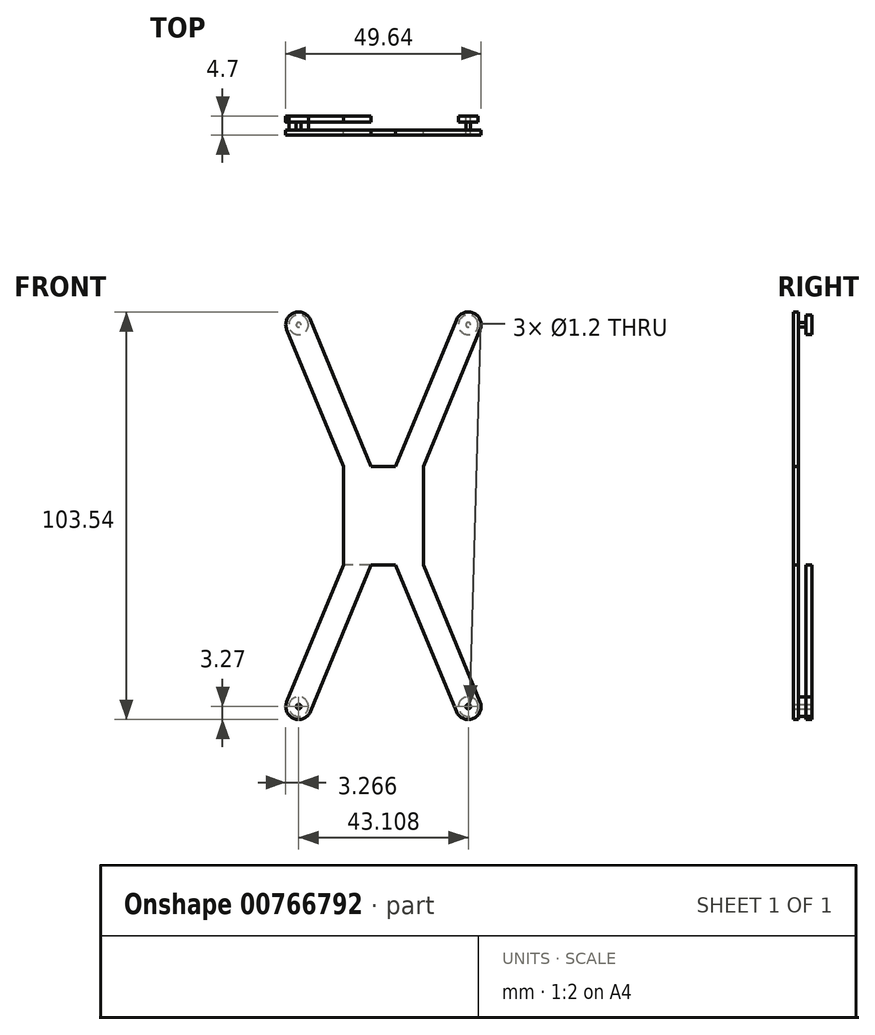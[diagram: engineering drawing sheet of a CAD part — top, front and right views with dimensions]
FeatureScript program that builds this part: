
annotation { "Feature Type Name" : "Feature", "Feature Type Description" : "" }
export const myFeature = defineFeature(function(context is Context, id is Id, definition is map)
    precondition{}
    {
        {
            var Q0;
            Q0=qCreatedBy(makeId("Front.planeOp"),FACE);
            var sketch = newSketch(context, id + "F0", { "sketchPlane" : qUnion([Q0])});
            skLineSegment(sketch, "E0", {"start": v(-5, 0) * mm, "end": v(-24.57, 47.25) * mm});
            skLineSegment(sketch, "E1", {"start": v(-24.57, 47.25) * mm, "end": v(-18.54, 49.75) * mm});
            skLineSegment(sketch, "E2", {"start": v(-18.54, 49.75) * mm, "end": v(0, 5) * mm});
            skLineSegment(sketch, "E3", {"start": v(0, 5) * mm, "end": v(18.54, 49.75) * mm});
            skLineSegment(sketch, "E4", {"start": v(18.54, 49.75) * mm, "end": v(24.57, 47.25) * mm});
            skLineSegment(sketch, "E5", {"start": v(24.57, 47.25) * mm, "end": v(5, 0) * mm});
            skLineSegment(sketch, "E6", {"start": v(5, 0) * mm, "end": v(24.57, -47.25) * mm});
            skLineSegment(sketch, "E7", {"start": v(24.57, -47.25) * mm, "end": v(18.54, -49.75) * mm});
            skLineSegment(sketch, "E8", {"start": v(18.54, -49.75) * mm, "end": v(0, -5) * mm});
            skLineSegment(sketch, "E9", {"start": v(0, -5) * mm, "end": v(-18.54, -49.75) * mm});
            skLineSegment(sketch, "E10", {"start": v(-18.54, -49.75) * mm, "end": v(-24.57, -47.25) * mm});
            skLineSegment(sketch, "E11", {"start": v(-24.57, -47.25) * mm, "end": v(-5, 0) * mm});
            skArc(sketch, "E12", {"start": v(-24.57, -47.25) * mm, "mid": v(-22.8, -51.52) * mm, "end": v(-18.54, -49.75) * mm});
            skArc(sketch, "E13", {"start": v(18.54, -49.75) * mm, "mid": v(22.8, -51.52) * mm, "end": v(24.57, -47.25) * mm});
            skArc(sketch, "E14", {"start": v(24.57, 47.25) * mm, "mid": v(22.8, 51.52) * mm, "end": v(18.54, 49.75) * mm});
            skArc(sketch, "E15", {"start": v(-18.54, 49.75) * mm, "mid": v(-22.8, 51.52) * mm, "end": v(-24.57, 47.25) * mm});
            skCircle(sketch, "E16", {"center": v(-21.55, 48.5) * mm, "radius": 0.6 * mm});
            skCircle(sketch, "E17", {"center": v(21.55, 48.5) * mm, "radius": 0.6 * mm});
            skCircle(sketch, "E18", {"center": v(-21.55, -48.5) * mm, "radius": 0.6 * mm});
            skCircle(sketch, "E19", {"center": v(21.55, -48.5) * mm, "radius": 0.6 * mm});
            skCircle(sketch, "E20", {"center": v(-21.55, -48.5) * mm, "radius": 2.5 * mm});
            skCircle(sketch, "E21", {"center": v(21.55, -48.5) * mm, "radius": 2.5 * mm});
            skCircle(sketch, "E22", {"center": v(-21.55, 48.5) * mm, "radius": 2.5 * mm});
            skCircle(sketch, "E23", {"center": v(21.55, 48.5) * mm, "radius": 2.5 * mm});
            skLineSegment(sketch, "E24.bottom", {"start": v(10.18, 12.5) * mm, "end": v(-10.18, 12.5) * mm});
            skLineSegment(sketch, "E24.top", {"start": v(10.18, -12.5) * mm, "end": v(-10.18, -12.5) * mm});
            skLineSegment(sketch, "E24.left", {"start": v(10.18, 12.5) * mm, "end": v(10.18, -12.5) * mm});
            skLineSegment(sketch, "E24.right", {"start": v(-10.18, 12.5) * mm, "end": v(-10.18, -12.5) * mm});
            skPoint(sketch, "E24.middle", {"position": v(0, 0) * mm});
            skSolve(sketch);
        }
        {
            var Q0;
            {var subQ0=sQuery(id+"F0.wireOp",EDGE,"E22");var subQ1=sQuery(id+"F0.wireOp",EDGE,"E1");var subQ2=makeQuery(id+"F0.imprint","INTERSECT",VERTEX,{"disambiguationData":[OD(0.0)],"derivedFrom":[subQ1,subQ0]});Q0=makeQuery(id+"F0.imprint","IMPRINT",FACE,{"disambiguationData":[TD([[makeQuery(id+"F0.imprint","IMPRINT",EDGE,{"disambiguationData":[TD([[subQ2,-1.0]])],"derivedFrom":subQ1}),1.0]])]});}
            var Q1;
            {var subQ0=sQuery(id+"F0.wireOp",EDGE,"E22");var subQ1=sQuery(id+"F0.wireOp",EDGE,"E1");var subQ2=makeQuery(id+"F0.imprint","INTERSECT",VERTEX,{"disambiguationData":[OD(0.0)],"derivedFrom":[subQ1,subQ0]});Q1=makeQuery(id+"F0.imprint","IMPRINT",FACE,{"disambiguationData":[TD([[makeQuery(id+"F0.imprint","IMPRINT",EDGE,{"disambiguationData":[TD([[subQ2,-1.0]])],"derivedFrom":subQ1}),-1.0]])]});}
            var Q2;
            {var subQ0=sQuery(id+"F0.wireOp",EDGE,"E16");var subQ1=sQuery(id+"F0.wireOp",EDGE,"E1");var subQ2=makeQuery(id+"F0.imprint","INTERSECT",VERTEX,{"disambiguationData":[OD(0.0)],"derivedFrom":[subQ1,subQ0]});Q2=makeQuery(id+"F0.imprint","IMPRINT",FACE,{"disambiguationData":[TD([[makeQuery(id+"F0.imprint","IMPRINT",EDGE,{"disambiguationData":[TD([[subQ2,-1.0]])],"derivedFrom":subQ1}),-1.0]])]});}
            var Q3;
            {var subQ0=sQuery(id+"F0.wireOp",EDGE,"E16");var subQ1=sQuery(id+"F0.wireOp",EDGE,"E1");var subQ2=makeQuery(id+"F0.imprint","INTERSECT",VERTEX,{"disambiguationData":[OD(0.0)],"derivedFrom":[subQ1,subQ0]});Q3=makeQuery(id+"F0.imprint","IMPRINT",FACE,{"disambiguationData":[TD([[makeQuery(id+"F0.imprint","IMPRINT",EDGE,{"disambiguationData":[TD([[subQ2,-1.0]])],"derivedFrom":subQ1}),1.0]])]});}
            var Q4;
            {var subQ0=sQuery(id+"F0.wireOp",EDGE,"E17");var subQ1=sQuery(id+"F0.wireOp",EDGE,"E4");var subQ2=makeQuery(id+"F0.imprint","INTERSECT",VERTEX,{"disambiguationData":[OD(0.0)],"derivedFrom":[subQ1,subQ0]});Q4=makeQuery(id+"F0.imprint","IMPRINT",FACE,{"disambiguationData":[TD([[makeQuery(id+"F0.imprint","IMPRINT",EDGE,{"disambiguationData":[TD([[subQ2,-1.0]])],"derivedFrom":subQ1}),1.0]])]});}
            var Q5;
            {var subQ0=sQuery(id+"F0.wireOp",EDGE,"E23");var subQ1=sQuery(id+"F0.wireOp",EDGE,"E4");var subQ2=makeQuery(id+"F0.imprint","INTERSECT",VERTEX,{"disambiguationData":[OD(0.0)],"derivedFrom":[subQ1,subQ0]});Q5=makeQuery(id+"F0.imprint","IMPRINT",FACE,{"disambiguationData":[TD([[makeQuery(id+"F0.imprint","IMPRINT",EDGE,{"disambiguationData":[TD([[subQ2,-1.0]])],"derivedFrom":subQ1}),1.0]])]});}
            var Q6;
            {var subQ0=sQuery(id+"F0.wireOp",EDGE,"E23");var subQ1=sQuery(id+"F0.wireOp",EDGE,"E4");var subQ2=makeQuery(id+"F0.imprint","INTERSECT",VERTEX,{"disambiguationData":[OD(0.0)],"derivedFrom":[subQ1,subQ0]});Q6=makeQuery(id+"F0.imprint","IMPRINT",FACE,{"disambiguationData":[TD([[makeQuery(id+"F0.imprint","IMPRINT",EDGE,{"disambiguationData":[TD([[subQ2,-1.0]])],"derivedFrom":subQ1}),-1.0]])]});}
            var Q7;
            {var subQ0=sQuery(id+"F0.wireOp",EDGE,"E17");var subQ1=sQuery(id+"F0.wireOp",EDGE,"E4");var subQ2=makeQuery(id+"F0.imprint","INTERSECT",VERTEX,{"disambiguationData":[OD(0.0)],"derivedFrom":[subQ1,subQ0]});Q7=makeQuery(id+"F0.imprint","IMPRINT",FACE,{"disambiguationData":[TD([[makeQuery(id+"F0.imprint","IMPRINT",EDGE,{"disambiguationData":[TD([[subQ2,-1.0]])],"derivedFrom":subQ1}),-1.0]])]});}
            var Q8;
            {var subQ0=sQuery(id+"F0.wireOp",EDGE,"E20");var subQ1=sQuery(id+"F0.wireOp",EDGE,"E10");var subQ2=makeQuery(id+"F0.imprint","INTERSECT",VERTEX,{"disambiguationData":[OD(0.0)],"derivedFrom":[subQ1,subQ0]});Q8=makeQuery(id+"F0.imprint","IMPRINT",FACE,{"disambiguationData":[TD([[makeQuery(id+"F0.imprint","IMPRINT",EDGE,{"disambiguationData":[TD([[subQ2,-1.0]])],"derivedFrom":subQ1}),1.0]])]});}
            var Q9;
            {var subQ0=sQuery(id+"F0.wireOp",EDGE,"E18");var subQ1=sQuery(id+"F0.wireOp",EDGE,"E10");var subQ2=makeQuery(id+"F0.imprint","INTERSECT",VERTEX,{"disambiguationData":[OD(0.0)],"derivedFrom":[subQ1,subQ0]});Q9=makeQuery(id+"F0.imprint","IMPRINT",FACE,{"disambiguationData":[TD([[makeQuery(id+"F0.imprint","IMPRINT",EDGE,{"disambiguationData":[TD([[subQ2,-1.0]])],"derivedFrom":subQ1}),1.0]])]});}
            var Q10;
            {var subQ0=sQuery(id+"F0.wireOp",EDGE,"E18");var subQ1=sQuery(id+"F0.wireOp",EDGE,"E10");var subQ2=makeQuery(id+"F0.imprint","INTERSECT",VERTEX,{"disambiguationData":[OD(0.0)],"derivedFrom":[subQ1,subQ0]});Q10=makeQuery(id+"F0.imprint","IMPRINT",FACE,{"disambiguationData":[TD([[makeQuery(id+"F0.imprint","IMPRINT",EDGE,{"disambiguationData":[TD([[subQ2,-1.0]])],"derivedFrom":subQ1}),-1.0]])]});}
            var Q11;
            {var subQ0=sQuery(id+"F0.wireOp",EDGE,"E20");var subQ1=sQuery(id+"F0.wireOp",EDGE,"E10");var subQ2=makeQuery(id+"F0.imprint","INTERSECT",VERTEX,{"disambiguationData":[OD(0.0)],"derivedFrom":[subQ1,subQ0]});Q11=makeQuery(id+"F0.imprint","IMPRINT",FACE,{"disambiguationData":[TD([[makeQuery(id+"F0.imprint","IMPRINT",EDGE,{"disambiguationData":[TD([[subQ2,-1.0]])],"derivedFrom":subQ1}),-1.0]])]});}
            var Q12;
            {var subQ0=sQuery(id+"F0.wireOp",EDGE,"E21");var subQ1=sQuery(id+"F0.wireOp",EDGE,"E7");var subQ2=makeQuery(id+"F0.imprint","INTERSECT",VERTEX,{"disambiguationData":[OD(0.0)],"derivedFrom":[subQ1,subQ0]});Q12=makeQuery(id+"F0.imprint","IMPRINT",FACE,{"disambiguationData":[TD([[makeQuery(id+"F0.imprint","IMPRINT",EDGE,{"disambiguationData":[TD([[subQ2,-1.0]])],"derivedFrom":subQ1}),-1.0]])]});}
            var Q13;
            {var subQ0=sQuery(id+"F0.wireOp",EDGE,"E21");var subQ1=sQuery(id+"F0.wireOp",EDGE,"E7");var subQ2=makeQuery(id+"F0.imprint","INTERSECT",VERTEX,{"disambiguationData":[OD(0.0)],"derivedFrom":[subQ1,subQ0]});Q13=makeQuery(id+"F0.imprint","IMPRINT",FACE,{"disambiguationData":[TD([[makeQuery(id+"F0.imprint","IMPRINT",EDGE,{"disambiguationData":[TD([[subQ2,-1.0]])],"derivedFrom":subQ1}),1.0]])]});}
            var Q14;
            {var subQ0=sQuery(id+"F0.wireOp",EDGE,"E19");var subQ1=sQuery(id+"F0.wireOp",EDGE,"E7");var subQ2=makeQuery(id+"F0.imprint","INTERSECT",VERTEX,{"disambiguationData":[OD(0.0)],"derivedFrom":[subQ1,subQ0]});Q14=makeQuery(id+"F0.imprint","IMPRINT",FACE,{"disambiguationData":[TD([[makeQuery(id+"F0.imprint","IMPRINT",EDGE,{"disambiguationData":[TD([[subQ2,-1.0]])],"derivedFrom":subQ1}),1.0]])]});}
            var Q15;
            {var subQ0=sQuery(id+"F0.wireOp",EDGE,"E19");var subQ1=sQuery(id+"F0.wireOp",EDGE,"E7");var subQ2=makeQuery(id+"F0.imprint","INTERSECT",VERTEX,{"disambiguationData":[OD(0.0)],"derivedFrom":[subQ1,subQ0]});Q15=makeQuery(id+"F0.imprint","IMPRINT",FACE,{"disambiguationData":[TD([[makeQuery(id+"F0.imprint","IMPRINT",EDGE,{"disambiguationData":[TD([[subQ2,-1.0]])],"derivedFrom":subQ1}),-1.0]])]});}
            var Q16;
            {var subQ11=sQuery(id+"F0.wireOp",EDGE,"E0");Q16=makeQuery(id+"F0.imprint","IMPRINT",FACE,{"disambiguationData":[TD([[makeQuery(id+"F0.imprint","IMPRINT",EDGE,{"derivedFrom":subQ11}),-1.0]])]});}
            var Q17;
            {var subQ0=sQuery(id+"F0.wireOp",EDGE,"E15");Q17=makeQuery(id+"F0.imprint","IMPRINT",FACE,{"disambiguationData":[TD([[makeQuery(id+"F0.imprint","IMPRINT",EDGE,{"derivedFrom":subQ0}),1.0]])]});}
            var Q18;
            {var subQ0=sQuery(id+"F0.wireOp",EDGE,"E14");Q18=makeQuery(id+"F0.imprint","IMPRINT",FACE,{"disambiguationData":[TD([[makeQuery(id+"F0.imprint","IMPRINT",EDGE,{"derivedFrom":subQ0}),1.0]])]});}
            var Q19;
            {var subQ0=sQuery(id+"F0.wireOp",EDGE,"E12");Q19=makeQuery(id+"F0.imprint","IMPRINT",FACE,{"disambiguationData":[TD([[makeQuery(id+"F0.imprint","IMPRINT",EDGE,{"derivedFrom":subQ0}),1.0]])]});}
            var Q20;
            {var subQ0=sQuery(id+"F0.wireOp",EDGE,"E13");Q20=makeQuery(id+"F0.imprint","IMPRINT",FACE,{"disambiguationData":[TD([[makeQuery(id+"F0.imprint","IMPRINT",EDGE,{"derivedFrom":subQ0}),1.0]])]});}
            var Q21;
            {var subQ3=sQuery(id+"F0.wireOp",EDGE,"E24.right");Q21=makeQuery(id+"F0.imprint","IMPRINT",FACE,{"disambiguationData":[TD([[makeQuery(id+"F0.imprint","IMPRINT",EDGE,{"derivedFrom":subQ3}),1.0]])]});}
            var Q22;
            {var subQ4=sQuery(id+"F0.wireOp",EDGE,"E2");var subQ13=sQuery(id+"F0.wireOp",EDGE,"E3");var subQ23=makeQuery(id+"F0.imprint","INTERSECT",VERTEX,{"derivedFrom":[subQ4,subQ13]});Q22=makeQuery(id+"F0.imprint","IMPRINT",FACE,{"disambiguationData":[TD([[makeQuery(id+"F0.imprint","IMPRINT",EDGE,{"disambiguationData":[TD([[subQ23,1.0]])],"derivedFrom":subQ4}),-1.0]])]});}
            var Q23;
            {var subQ0=sQuery(id+"F0.wireOp",EDGE,"E3");var subQ1=sQuery(id+"F0.wireOp",EDGE,"E2");var subQ2=makeQuery(id+"F0.imprint","INTERSECT",VERTEX,{"derivedFrom":[subQ1,subQ0]});Q23=makeQuery(id+"F0.imprint","IMPRINT",FACE,{"disambiguationData":[TD([[makeQuery(id+"F0.imprint","IMPRINT",EDGE,{"disambiguationData":[TD([[subQ2,1.0]])],"derivedFrom":subQ1}),1.0]])]});}
            var Q24;
            {var subQ2=sQuery(id+"F0.wireOp",EDGE,"E4");var subQ8=sQuery(id+"F0.wireOp",EDGE,"E23");var subQ9=makeQuery(id+"F0.imprint","INTERSECT",VERTEX,{"disambiguationData":[OD(0.0)],"derivedFrom":[subQ2,subQ8]});Q24=makeQuery(id+"F0.imprint","IMPRINT",FACE,{"disambiguationData":[TD([[makeQuery(id+"F0.imprint","IMPRINT",EDGE,{"disambiguationData":[TD([[subQ9,-1.0]])],"derivedFrom":subQ8}),-1.0]])]});}
            var Q25;
            {var subQ3=sQuery(id+"F0.wireOp",EDGE,"E24.left");Q25=makeQuery(id+"F0.imprint","IMPRINT",FACE,{"disambiguationData":[TD([[makeQuery(id+"F0.imprint","IMPRINT",EDGE,{"derivedFrom":subQ3}),-1.0]])]});}
            var Q26;
            {var subQ0=sQuery(id+"F0.wireOp",EDGE,"E9");var subQ1=sQuery(id+"F0.wireOp",EDGE,"E8");var subQ2=makeQuery(id+"F0.imprint","INTERSECT",VERTEX,{"derivedFrom":[subQ1,subQ0]});Q26=makeQuery(id+"F0.imprint","IMPRINT",FACE,{"disambiguationData":[TD([[makeQuery(id+"F0.imprint","IMPRINT",EDGE,{"disambiguationData":[TD([[subQ2,1.0]])],"derivedFrom":subQ1}),1.0]])]});}
            var Q27;
            {var subQ2=sQuery(id+"F0.wireOp",EDGE,"E7");var subQ8=sQuery(id+"F0.wireOp",EDGE,"E21");var subQ9=makeQuery(id+"F0.imprint","INTERSECT",VERTEX,{"disambiguationData":[OD(0.0)],"derivedFrom":[subQ2,subQ8]});Q27=makeQuery(id+"F0.imprint","IMPRINT",FACE,{"disambiguationData":[TD([[makeQuery(id+"F0.imprint","IMPRINT",EDGE,{"disambiguationData":[TD([[subQ9,-1.0]])],"derivedFrom":subQ8}),-1.0]])]});}
            var Q28;
            {var subQ2=sQuery(id+"F0.wireOp",EDGE,"E10");var subQ8=sQuery(id+"F0.wireOp",EDGE,"E20");var subQ9=makeQuery(id+"F0.imprint","INTERSECT",VERTEX,{"disambiguationData":[OD(0.0)],"derivedFrom":[subQ2,subQ8]});Q28=makeQuery(id+"F0.imprint","IMPRINT",FACE,{"disambiguationData":[TD([[makeQuery(id+"F0.imprint","IMPRINT",EDGE,{"disambiguationData":[TD([[subQ9,-1.0]])],"derivedFrom":subQ8}),-1.0]])]});}
            extrude(context, id + "F1", {"entities" : qUnion([Q0, Q1, Q2, Q3, Q4, Q5, Q6, Q7, Q8, Q9, Q10, Q11, Q12, Q13, Q14, Q15, Q16, Q17, Q18, Q19, Q20, Q21, Q22, Q23, Q24, Q25, Q26, Q27, Q28]), "depth" : 1.2 * mm, "offsetDistance" : 25 * mm});
        }
        {
            var Q0;
            {var subQ0=sQuery(id+"F0.wireOp",EDGE,"E23");var subQ1=sQuery(id+"F0.wireOp",EDGE,"E4");var subQ2=makeQuery(id+"F0.imprint","INTERSECT",VERTEX,{"disambiguationData":[OD(0.0)],"derivedFrom":[subQ1,subQ0]});Q0=makeQuery(id+"F0.imprint","IMPRINT",FACE,{"disambiguationData":[TD([[makeQuery(id+"F0.imprint","IMPRINT",EDGE,{"disambiguationData":[TD([[subQ2,-1.0]])],"derivedFrom":subQ1}),1.0]])]});}
            var Q1;
            {var subQ0=sQuery(id+"F0.wireOp",EDGE,"E23");var subQ1=sQuery(id+"F0.wireOp",EDGE,"E4");var subQ2=makeQuery(id+"F0.imprint","INTERSECT",VERTEX,{"disambiguationData":[OD(0.0)],"derivedFrom":[subQ1,subQ0]});Q1=makeQuery(id+"F0.imprint","IMPRINT",FACE,{"disambiguationData":[TD([[makeQuery(id+"F0.imprint","IMPRINT",EDGE,{"disambiguationData":[TD([[subQ2,-1.0]])],"derivedFrom":subQ1}),-1.0]])]});}
            var Q2;
            {var subQ0=sQuery(id+"F0.wireOp",EDGE,"E22");var subQ1=sQuery(id+"F0.wireOp",EDGE,"E1");var subQ2=makeQuery(id+"F0.imprint","INTERSECT",VERTEX,{"disambiguationData":[OD(0.0)],"derivedFrom":[subQ1,subQ0]});Q2=makeQuery(id+"F0.imprint","IMPRINT",FACE,{"disambiguationData":[TD([[makeQuery(id+"F0.imprint","IMPRINT",EDGE,{"disambiguationData":[TD([[subQ2,-1.0]])],"derivedFrom":subQ1}),1.0]])]});}
            var Q3;
            {var subQ0=sQuery(id+"F0.wireOp",EDGE,"E22");var subQ1=sQuery(id+"F0.wireOp",EDGE,"E1");var subQ2=makeQuery(id+"F0.imprint","INTERSECT",VERTEX,{"disambiguationData":[OD(0.0)],"derivedFrom":[subQ1,subQ0]});Q3=makeQuery(id+"F0.imprint","IMPRINT",FACE,{"disambiguationData":[TD([[makeQuery(id+"F0.imprint","IMPRINT",EDGE,{"disambiguationData":[TD([[subQ2,-1.0]])],"derivedFrom":subQ1}),-1.0]])]});}
            var Q4;
            {var subQ0=sQuery(id+"F0.wireOp",EDGE,"E20");var subQ1=sQuery(id+"F0.wireOp",EDGE,"E10");var subQ2=makeQuery(id+"F0.imprint","INTERSECT",VERTEX,{"disambiguationData":[OD(0.0)],"derivedFrom":[subQ1,subQ0]});Q4=makeQuery(id+"F0.imprint","IMPRINT",FACE,{"disambiguationData":[TD([[makeQuery(id+"F0.imprint","IMPRINT",EDGE,{"disambiguationData":[TD([[subQ2,-1.0]])],"derivedFrom":subQ1}),-1.0]])]});}
            var Q5;
            {var subQ0=sQuery(id+"F0.wireOp",EDGE,"E20");var subQ1=sQuery(id+"F0.wireOp",EDGE,"E10");var subQ2=makeQuery(id+"F0.imprint","INTERSECT",VERTEX,{"disambiguationData":[OD(0.0)],"derivedFrom":[subQ1,subQ0]});Q5=makeQuery(id+"F0.imprint","IMPRINT",FACE,{"disambiguationData":[TD([[makeQuery(id+"F0.imprint","IMPRINT",EDGE,{"disambiguationData":[TD([[subQ2,-1.0]])],"derivedFrom":subQ1}),1.0]])]});}
            var Q6;
            {var subQ0=sQuery(id+"F0.wireOp",EDGE,"E21");var subQ1=sQuery(id+"F0.wireOp",EDGE,"E7");var subQ2=makeQuery(id+"F0.imprint","INTERSECT",VERTEX,{"disambiguationData":[OD(0.0)],"derivedFrom":[subQ1,subQ0]});Q6=makeQuery(id+"F0.imprint","IMPRINT",FACE,{"disambiguationData":[TD([[makeQuery(id+"F0.imprint","IMPRINT",EDGE,{"disambiguationData":[TD([[subQ2,-1.0]])],"derivedFrom":subQ1}),1.0]])]});}
            var Q7;
            {var subQ0=sQuery(id+"F0.wireOp",EDGE,"E21");var subQ1=sQuery(id+"F0.wireOp",EDGE,"E7");var subQ2=makeQuery(id+"F0.imprint","INTERSECT",VERTEX,{"disambiguationData":[OD(0.0)],"derivedFrom":[subQ1,subQ0]});Q7=makeQuery(id+"F0.imprint","IMPRINT",FACE,{"disambiguationData":[TD([[makeQuery(id+"F0.imprint","IMPRINT",EDGE,{"disambiguationData":[TD([[subQ2,-1.0]])],"derivedFrom":subQ1}),-1.0]])]});}
            var Q8;
            {var subQ0=sQuery(id+"F0.wireOp",EDGE,"E19");var subQ1=sQuery(id+"F0.wireOp",EDGE,"E7");var subQ2=makeQuery(id+"F0.imprint","INTERSECT",VERTEX,{"disambiguationData":[OD(0.0)],"derivedFrom":[subQ1,subQ0]});Q8=makeQuery(id+"F0.imprint","IMPRINT",FACE,{"disambiguationData":[TD([[makeQuery(id+"F0.imprint","IMPRINT",EDGE,{"disambiguationData":[TD([[subQ2,-1.0]])],"derivedFrom":subQ1}),1.0]])]});}
            var Q9;
            {var subQ0=sQuery(id+"F0.wireOp",EDGE,"E19");var subQ1=sQuery(id+"F0.wireOp",EDGE,"E7");var subQ2=makeQuery(id+"F0.imprint","INTERSECT",VERTEX,{"disambiguationData":[OD(0.0)],"derivedFrom":[subQ1,subQ0]});Q9=makeQuery(id+"F0.imprint","IMPRINT",FACE,{"disambiguationData":[TD([[makeQuery(id+"F0.imprint","IMPRINT",EDGE,{"disambiguationData":[TD([[subQ2,-1.0]])],"derivedFrom":subQ1}),-1.0]])]});}
            var Q10;
            {var subQ0=sQuery(id+"F0.wireOp",EDGE,"E17");var subQ1=sQuery(id+"F0.wireOp",EDGE,"E4");var subQ2=makeQuery(id+"F0.imprint","INTERSECT",VERTEX,{"disambiguationData":[OD(0.0)],"derivedFrom":[subQ1,subQ0]});Q10=makeQuery(id+"F0.imprint","IMPRINT",FACE,{"disambiguationData":[TD([[makeQuery(id+"F0.imprint","IMPRINT",EDGE,{"disambiguationData":[TD([[subQ2,-1.0]])],"derivedFrom":subQ1}),1.0]])]});}
            var Q11;
            {var subQ0=sQuery(id+"F0.wireOp",EDGE,"E17");var subQ1=sQuery(id+"F0.wireOp",EDGE,"E4");var subQ2=makeQuery(id+"F0.imprint","INTERSECT",VERTEX,{"disambiguationData":[OD(0.0)],"derivedFrom":[subQ1,subQ0]});Q11=makeQuery(id+"F0.imprint","IMPRINT",FACE,{"disambiguationData":[TD([[makeQuery(id+"F0.imprint","IMPRINT",EDGE,{"disambiguationData":[TD([[subQ2,-1.0]])],"derivedFrom":subQ1}),-1.0]])]});}
            var Q12;
            {var subQ0=sQuery(id+"F0.wireOp",EDGE,"E16");var subQ1=sQuery(id+"F0.wireOp",EDGE,"E1");var subQ2=makeQuery(id+"F0.imprint","INTERSECT",VERTEX,{"disambiguationData":[OD(0.0)],"derivedFrom":[subQ1,subQ0]});Q12=makeQuery(id+"F0.imprint","IMPRINT",FACE,{"disambiguationData":[TD([[makeQuery(id+"F0.imprint","IMPRINT",EDGE,{"disambiguationData":[TD([[subQ2,-1.0]])],"derivedFrom":subQ1}),-1.0]])]});}
            var Q13;
            {var subQ0=sQuery(id+"F0.wireOp",EDGE,"E16");var subQ1=sQuery(id+"F0.wireOp",EDGE,"E1");var subQ2=makeQuery(id+"F0.imprint","INTERSECT",VERTEX,{"disambiguationData":[OD(0.0)],"derivedFrom":[subQ1,subQ0]});Q13=makeQuery(id+"F0.imprint","IMPRINT",FACE,{"disambiguationData":[TD([[makeQuery(id+"F0.imprint","IMPRINT",EDGE,{"disambiguationData":[TD([[subQ2,-1.0]])],"derivedFrom":subQ1}),1.0]])]});}
            var Q14;
            {var subQ0=sQuery(id+"F0.wireOp",EDGE,"E18");var subQ1=sQuery(id+"F0.wireOp",EDGE,"E10");var subQ2=makeQuery(id+"F0.imprint","INTERSECT",VERTEX,{"disambiguationData":[OD(0.0)],"derivedFrom":[subQ1,subQ0]});Q14=makeQuery(id+"F0.imprint","IMPRINT",FACE,{"disambiguationData":[TD([[makeQuery(id+"F0.imprint","IMPRINT",EDGE,{"disambiguationData":[TD([[subQ2,-1.0]])],"derivedFrom":subQ1}),-1.0]])]});}
            var Q15;
            {var subQ0=sQuery(id+"F0.wireOp",EDGE,"E18");var subQ1=sQuery(id+"F0.wireOp",EDGE,"E10");var subQ2=makeQuery(id+"F0.imprint","INTERSECT",VERTEX,{"disambiguationData":[OD(0.0)],"derivedFrom":[subQ1,subQ0]});Q15=makeQuery(id+"F0.imprint","IMPRINT",FACE,{"disambiguationData":[TD([[makeQuery(id+"F0.imprint","IMPRINT",EDGE,{"disambiguationData":[TD([[subQ2,-1.0]])],"derivedFrom":subQ1}),1.0]])]});}
            extrude(context, id + "F2", {"entities" : qUnion([Q0, Q1, Q2, Q3, Q4, Q5, Q6, Q7, Q8, Q9, Q10, Q11, Q12, Q13, Q14, Q15]), "operationType" : NewBodyOperationType.ADD, "oppositeDirection" : true, "depth" : 3.5 * mm, "offsetDistance" : 25 * mm});
        }
        {
            var Q0;
            {var subQ0=sQuery(id+"F0.wireOp",EDGE,"E22");var subQ1=sQuery(id+"F0.wireOp",EDGE,"E1");var subQ2=makeQuery(id+"F0.imprint","INTERSECT",VERTEX,{"disambiguationData":[OD(0.0)],"derivedFrom":[subQ1,subQ0]});Q0=makeQuery(id+"F0.imprint","IMPRINT",FACE,{"disambiguationData":[TD([[makeQuery(id+"F0.imprint","IMPRINT",EDGE,{"disambiguationData":[TD([[subQ2,-1.0]])],"derivedFrom":subQ1}),1.0]])]});}
            var Q1;
            {var subQ0=sQuery(id+"F0.wireOp",EDGE,"E22");var subQ1=sQuery(id+"F0.wireOp",EDGE,"E1");var subQ2=makeQuery(id+"F0.imprint","INTERSECT",VERTEX,{"disambiguationData":[OD(0.0)],"derivedFrom":[subQ1,subQ0]});Q1=makeQuery(id+"F0.imprint","IMPRINT",FACE,{"disambiguationData":[TD([[makeQuery(id+"F0.imprint","IMPRINT",EDGE,{"disambiguationData":[TD([[subQ2,-1.0]])],"derivedFrom":subQ1}),-1.0]])]});}
            var Q2;
            {var subQ0=sQuery(id+"F0.wireOp",EDGE,"E23");var subQ1=sQuery(id+"F0.wireOp",EDGE,"E4");var subQ2=makeQuery(id+"F0.imprint","INTERSECT",VERTEX,{"disambiguationData":[OD(0.0)],"derivedFrom":[subQ1,subQ0]});Q2=makeQuery(id+"F0.imprint","IMPRINT",FACE,{"disambiguationData":[TD([[makeQuery(id+"F0.imprint","IMPRINT",EDGE,{"disambiguationData":[TD([[subQ2,-1.0]])],"derivedFrom":subQ1}),1.0]])]});}
            var Q3;
            {var subQ0=sQuery(id+"F0.wireOp",EDGE,"E23");var subQ1=sQuery(id+"F0.wireOp",EDGE,"E4");var subQ2=makeQuery(id+"F0.imprint","INTERSECT",VERTEX,{"disambiguationData":[OD(0.0)],"derivedFrom":[subQ1,subQ0]});Q3=makeQuery(id+"F0.imprint","IMPRINT",FACE,{"disambiguationData":[TD([[makeQuery(id+"F0.imprint","IMPRINT",EDGE,{"disambiguationData":[TD([[subQ2,-1.0]])],"derivedFrom":subQ1}),-1.0]])]});}
            var Q4;
            {var subQ0=sQuery(id+"F0.wireOp",EDGE,"E21");var subQ1=sQuery(id+"F0.wireOp",EDGE,"E7");var subQ2=makeQuery(id+"F0.imprint","INTERSECT",VERTEX,{"disambiguationData":[OD(0.0)],"derivedFrom":[subQ1,subQ0]});Q4=makeQuery(id+"F0.imprint","IMPRINT",FACE,{"disambiguationData":[TD([[makeQuery(id+"F0.imprint","IMPRINT",EDGE,{"disambiguationData":[TD([[subQ2,-1.0]])],"derivedFrom":subQ1}),-1.0]])]});}
            var Q5;
            {var subQ0=sQuery(id+"F0.wireOp",EDGE,"E21");var subQ1=sQuery(id+"F0.wireOp",EDGE,"E7");var subQ2=makeQuery(id+"F0.imprint","INTERSECT",VERTEX,{"disambiguationData":[OD(0.0)],"derivedFrom":[subQ1,subQ0]});Q5=makeQuery(id+"F0.imprint","IMPRINT",FACE,{"disambiguationData":[TD([[makeQuery(id+"F0.imprint","IMPRINT",EDGE,{"disambiguationData":[TD([[subQ2,-1.0]])],"derivedFrom":subQ1}),1.0]])]});}
            var Q6;
            {var subQ0=sQuery(id+"F0.wireOp",EDGE,"E20");var subQ1=sQuery(id+"F0.wireOp",EDGE,"E10");var subQ2=makeQuery(id+"F0.imprint","INTERSECT",VERTEX,{"disambiguationData":[OD(0.0)],"derivedFrom":[subQ1,subQ0]});Q6=makeQuery(id+"F0.imprint","IMPRINT",FACE,{"disambiguationData":[TD([[makeQuery(id+"F0.imprint","IMPRINT",EDGE,{"disambiguationData":[TD([[subQ2,-1.0]])],"derivedFrom":subQ1}),1.0]])]});}
            var Q7;
            {var subQ0=sQuery(id+"F0.wireOp",EDGE,"E20");var subQ1=sQuery(id+"F0.wireOp",EDGE,"E10");var subQ2=makeQuery(id+"F0.imprint","INTERSECT",VERTEX,{"disambiguationData":[OD(0.0)],"derivedFrom":[subQ1,subQ0]});Q7=makeQuery(id+"F0.imprint","IMPRINT",FACE,{"disambiguationData":[TD([[makeQuery(id+"F0.imprint","IMPRINT",EDGE,{"disambiguationData":[TD([[subQ2,-1.0]])],"derivedFrom":subQ1}),-1.0]])]});}
            extrude(context, id + "F3", {"entities" : qUnion([Q0, Q1, Q2, Q3, Q4, Q5, Q6, Q7]), "operationType" : NewBodyOperationType.REMOVE, "oppositeDirection" : true, "depth" : 2 * mm, "offsetDistance" : 25 * mm});
        }
    });
